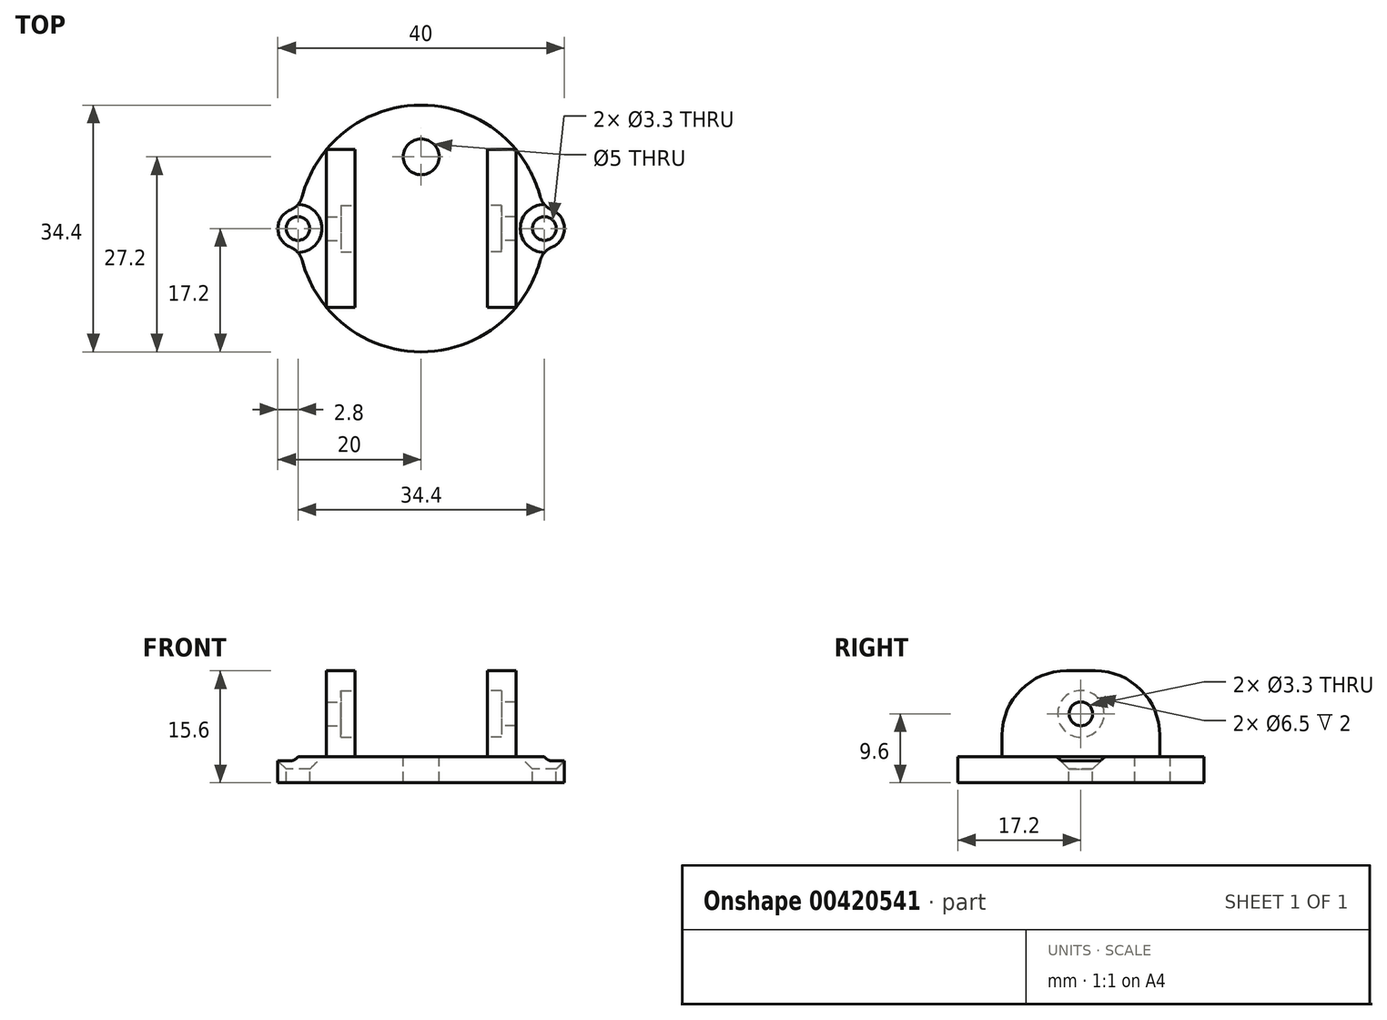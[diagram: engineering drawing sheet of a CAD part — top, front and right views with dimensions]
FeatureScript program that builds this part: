
annotation { "Feature Type Name" : "Feature", "Feature Type Description" : "" }
export const myFeature = defineFeature(function(context is Context, id is Id, definition is map)
    precondition{}
    {
        {
            var Q0;
            Q0=qCreatedBy(makeId("Top.planeOp"),FACE);
            var sketch = newSketch(context, id + "F0", { "sketchPlane" : qUnion([Q0])});
            skArc(sketch, "E0", {"start": v(16.97, 2.8) * mm, "mid": v(0, 17.2) * mm, "end": v(-16.97, 2.8) * mm});
            skArc(sketch, "E1", {"start": v(-16.97, 2.8) * mm, "mid": v(-20, 0) * mm, "end": v(-16.97, -2.8) * mm});
            skArc(sketch, "E2", {"start": v(16.97, -2.8) * mm, "mid": v(20, 0) * mm, "end": v(16.97, 2.8) * mm});
            skArc(sketch, "E3.trimOffspring", {"start": v(-16.97, -2.8) * mm, "mid": v(0, -17.2) * mm, "end": v(16.97, -2.8) * mm});
            skSolve(sketch);
        }
        {
            var Q0;
            Q0=makeQuery(id+"F0.imprint","IMPRINT",FACE,{"disambiguationData":[TD([[makeQuery(id+"F0.imprint","IMPRINT",EDGE,{"derivedFrom":sQuery(id+"F0.wireOp",EDGE,"E0")}),1.0]])]});
            extrude(context, id + "F1", {"entities" : qUnion([Q0]), "depth" : 3.6 * mm});
        }
        {
            var Q0;
            Q0=makeQuery(id+"F1.opExtrude","SWEPT_EDGE",EDGE,{"disambiguationData":[OSD([sQuery(id+"F0.wireOp",EDGE,"E1"),sQuery(id+"F0.wireOp",EDGE,"E3.trimOffspring")])]});
            var Q1;
            Q1=makeQuery(id+"F1.opExtrude","SWEPT_EDGE",EDGE,{"disambiguationData":[OSD([sQuery(id+"F0.wireOp",EDGE,"E2"),sQuery(id+"F0.wireOp",EDGE,"E3.trimOffspring")])]});
            var Q2;
            Q2=makeQuery(id+"F1.opExtrude","SWEPT_EDGE",EDGE,{"disambiguationData":[OSD([sQuery(id+"F0.wireOp",EDGE,"E0"),sQuery(id+"F0.wireOp",EDGE,"E2")])]});
            var Q3;
            Q3=makeQuery(id+"F1.opExtrude","SWEPT_EDGE",EDGE,{"disambiguationData":[OSD([sQuery(id+"F0.wireOp",EDGE,"E0"),sQuery(id+"F0.wireOp",EDGE,"E1")])]});
            fillet(context, id + "F2", {"entities" : qUnion([Q0, Q1, Q2, Q3]), "radius" : 2.8 * mm, "tangentPropagation" : true, "allowEdgeOverflow" : false});
        }
        {
            var Q0;
            Q0=makeQuery(id+"F1.opExtrude","CAP_FACE",FACE,{"disambiguationData":[OSD([sQuery(id+"F0.wireOp",EDGE,"E0"),sQuery(id+"F0.wireOp",EDGE,"E1"),sQuery(id+"F0.wireOp",EDGE,"E2"),sQuery(id+"F0.wireOp",EDGE,"E3.trimOffspring")])],"isStart":false});
            var sketch = newSketch(context, id + "F3", { "sketchPlane" : qUnion([Q0])});
            skPoint(sketch, "E4", {"position": v(-17.2, 0) * mm});
            skPoint(sketch, "E5", {"position": v(17.2, 0) * mm});
            skCircle(sketch, "E6", {"center": v(0, 10) * mm, "radius": 2.5 * mm});
            skLineSegment(sketch, "E7.bottom", {"start": v(-13.22, 11) * mm, "end": v(-9.22, 11) * mm});
            skLineSegment(sketch, "E7.top", {"start": v(-13.22, -11) * mm, "end": v(-9.22, -11) * mm});
            skLineSegment(sketch, "E7.left", {"start": v(-13.22, 11) * mm, "end": v(-13.22, -11) * mm});
            skLineSegment(sketch, "E7.right", {"start": v(-9.22, 11) * mm, "end": v(-9.22, -11) * mm});
            skPoint(sketch, "E7.middle", {"position": v(-11.22, 0) * mm});
            skLineSegment(sketch, "E8.bottom", {"start": v(13.22, -11) * mm, "end": v(9.22, -11) * mm});
            skLineSegment(sketch, "E8.top", {"start": v(13.22, 11) * mm, "end": v(9.22, 11) * mm});
            skLineSegment(sketch, "E8.left", {"start": v(13.22, -11) * mm, "end": v(13.22, 11) * mm});
            skLineSegment(sketch, "E8.right", {"start": v(9.22, -11) * mm, "end": v(9.22, 11) * mm});
            skPoint(sketch, "E8.middle", {"position": v(11.22, 0) * mm});
            skSolve(sketch);
        }
        {
            var Q0;
            Q0=sQuery(id+"F3.wireOp",VERTEX,"E4");
            var Q1;
            Q1=sQuery(id+"F3.wireOp",VERTEX,"E5");
            var Q2;
            Q2=makeQuery(id+"F1.opExtrude","SWEPT_BODY",BODY,{"disambiguationData":[OSD([sQuery(id+"F0.wireOp",EDGE,"E0"),sQuery(id+"F0.wireOp",EDGE,"E1"),sQuery(id+"F0.wireOp",EDGE,"E2"),sQuery(id+"F0.wireOp",EDGE,"E3.trimOffspring")])]});
            hole(context, id + "F4", {"style" : HoleStyle.C_SINK, "endStyle" : HoleEndStyle.BLIND, "standardTappedOrClearance" : lookupTablePath({ "standard" : "ISO", "fit" : "Normal", "size" : "M3", "type" : "Clearance" }), "standardBlindInLast" : lookupTablePath({ "fit" : "Standard", "standard" : "ISO", "size" : "M3", "type" : "Clearance" }), "holeDiameter" : 3.3 * mm, "cSinkDiameter" : 6.72 * mm, "cSinkAngle" : 90 * degree, "holeDepth" : 20 * mm, "isTappedThrough" : true, "tappedDepth" : 12 * mm, "tapClearance" : 3, "locations" : qUnion([Q0, Q1]), "scope" : qUnion([Q2])});
        }
        {
            var Q0;
            Q0=makeQuery(id+"F3.imprint","IMPRINT",FACE,{"disambiguationData":[TD([[makeQuery(id+"F3.imprint","IMPRINT",EDGE,{"derivedFrom":sQuery(id+"F3.wireOp",EDGE,"E6")}),1.0]])]});
            extrude(context, id + "F5", {"entities" : qUnion([Q0]), "operationType" : NewBodyOperationType.REMOVE, "endBound" : BoundingType.UP_TO_NEXT, "oppositeDirection" : true, "depth" : 25 * mm});
        }
        {
            var Q0;
            Q0=makeQuery(id+"F3.imprint","IMPRINT",FACE,{"disambiguationData":[TD([[makeQuery(id+"F3.imprint","IMPRINT",EDGE,{"derivedFrom":sQuery(id+"F3.wireOp",EDGE,"E7.bottom")}),-1.0]])]});
            var Q1;
            Q1=makeQuery(id+"F3.imprint","IMPRINT",FACE,{"disambiguationData":[TD([[makeQuery(id+"F3.imprint","IMPRINT",EDGE,{"derivedFrom":sQuery(id+"F3.wireOp",EDGE,"E8.bottom")}),-1.0]])]});
            extrude(context, id + "F6", {"entities" : qUnion([Q0, Q1]), "operationType" : NewBodyOperationType.ADD, "depth" : 12 * mm});
        }
        {
            var Q0;
            Q0=makeQuery(id+"F6.opExtrude","SWEPT_FACE",FACE,{"disambiguationData":[OSD([sQuery(id+"F3.wireOp",EDGE,"E7.right")])]});
            var sketch = newSketch(context, id + "F7", { "sketchPlane" : qUnion([Q0])});
            skPoint(sketch, "E9", {"position": v(0, 9.6) * mm});
            skPoint(sketch, "E9.positionSnap0", {"position": v(-11, 9.6) * mm});
            skPoint(sketch, "E9.positionSnap1", {"position": v(0, 15.6) * mm});
            skSolve(sketch);
        }
        {
            var Q0;
            Q0=makeQuery(id+"F6.opExtrude","SWEPT_FACE",FACE,{"disambiguationData":[OSD([sQuery(id+"F3.wireOp",EDGE,"E8.right")])]});
            var sketch = newSketch(context, id + "F8", { "sketchPlane" : qUnion([Q0])});
            skPoint(sketch, "E10", {"position": v(0, 9.6) * mm});
            skPoint(sketch, "E10.positionSnap0", {"position": v(0, 15.6) * mm});
            skPoint(sketch, "E10.positionSnap1", {"position": v(-11, 9.6) * mm});
            skSolve(sketch);
        }
        {
            var Q0;
            Q0=sQuery(id+"F8.wireOp",VERTEX,"E10");
            var Q1;
            Q1=sQuery(id+"F7.wireOp",VERTEX,"E9");
            var Q2;
            Q2=makeQuery(id+"F1.opExtrude","SWEPT_BODY",BODY,{"disambiguationData":[OSD([sQuery(id+"F0.wireOp",EDGE,"E0"),sQuery(id+"F0.wireOp",EDGE,"E1"),sQuery(id+"F0.wireOp",EDGE,"E2"),sQuery(id+"F0.wireOp",EDGE,"E3.trimOffspring")])]});
            hole(context, id + "F9", {"style" : HoleStyle.C_BORE, "endStyle" : HoleEndStyle.BLIND, "holeDiameter" : 3.3 * mm, "cBoreDiameter" : 6.5 * mm, "cBoreDepth" : 2 * mm, "holeDepth" : 20 * mm, "isTappedThrough" : true, "tappedDepth" : 12 * mm, "tapClearance" : 3, "locations" : qUnion([Q0, Q1]), "scope" : qUnion([Q2])});
        }
        {
            var Q0;
            Q0=makeQuery(id+"F6.opExtrude","CAP_EDGE",EDGE,{"disambiguationData":[OSD([sQuery(id+"F3.wireOp",EDGE,"E8.top")])],"isStart":false});
            var Q1;
            Q1=makeQuery(id+"F6.opExtrude","CAP_EDGE",EDGE,{"disambiguationData":[OSD([sQuery(id+"F3.wireOp",EDGE,"E7.bottom")])],"isStart":false});
            var Q2;
            Q2=makeQuery(id+"F6.opExtrude","CAP_EDGE",EDGE,{"disambiguationData":[OSD([sQuery(id+"F3.wireOp",EDGE,"E7.top")])],"isStart":false});
            var Q3;
            Q3=makeQuery(id+"F6.opExtrude","CAP_EDGE",EDGE,{"disambiguationData":[OSD([sQuery(id+"F3.wireOp",EDGE,"E8.bottom")])],"isStart":false});
            fillet(context, id + "F10", {"entities" : qUnion([Q0, Q1, Q2, Q3]), "radius" : 9 * mm, "tangentPropagation" : true, "allowEdgeOverflow" : false});
        }
    });
